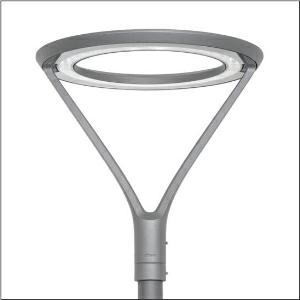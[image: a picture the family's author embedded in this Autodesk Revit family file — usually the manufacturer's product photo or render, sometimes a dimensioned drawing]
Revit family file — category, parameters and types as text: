
# Revit family: dl_r__20___pl1_2s_5xa512832s008p_c84b
name_source: partatom
category: Lighting Fixtures
units: mm (PartAtom-declared; Revit-internal decimal feet)

## family parameters
Cut with Voids When Loaded = No
Host = Face
Light Source = No
Part Type = Normal
Room Calculation Point = No
Round Connector Dimension = Use Diameter
Shared = No

## types (1)
- --- (1 x LED, 4250 lm, 43.6 W, 2200K)
    Apparent Load = 44 VA
    CIE Flux Codes = 33 78 99 100 100
    Color Rendering = 70
    Color Temperature = 2200K
    Default Elevation = 1800 mm
    Description = DL® 20, mast luminaire, primary light control with reflector, highly specular, primary optical cover: cover, of toughened safety glass of clear glass with excellent transmission level, light distribution: PL1.2s, light emission: direct distribution, primary light characteristic: symmetric, installation type: post-top, LED, High Power LED, rated luminous flux: 4.210lm, luminous efficacy: 80lm/W, light colour: 722, colour temperature: 2200K, control gear: ECG Plus, control: flexible luminous flux parameterisation, time-dependent luminous flux control, constant luminous flux control, digital communication interface, power reduction, overheat protection, electronic power reduction, mains connection: 230..240V, 50/60Hz, connection cable pre-assembled, cable length: 5m, start of lifetime: 53W, end of service life: 54W, reduction: 24W, luminaire housing, upper part, of cast aluminium, powder-coated, Siteco® metallic grey (DB 702S), diameter: 690mm, height: 690mm, spigot size: 76mm (post-top), luminaire housing, of cast aluminium, powder-coated, Siteco® metallic grey (DB 702S), equipment: Power, protection rating (complete): IP66, insulation class (complete): insulation class II (safety insulation), certification: CE, ENEC, VDE, impact resistance: IK08, permissible operating ambient temperature: -25..+30°C, standard-compliant lighting for roads and squares, packaging unit: 1 piece

Light Distribution: PL1.2s
    Height = 690 mm
    Lamp = 1 x LED
    Lamp Light Flux = 4250 lm
    Lamp Power = 43.6 W
    Lamp count = 1
    Length = 690 mm
    Luminous efficacy = 97 lm/W
    Manufacturer = Siteco
    ModVariant = No
    Model = 5XA512832S008P
    Number of Poles = 1
    OnlyDefault = Yes
    Power Factor = 1
    Product Name = DL® 20 | PL1.2s
    Product group = mast luminaire | pylon top
    ProductGroupID = 6100
    Protection Class = Protection class II
    Protection Degree = IP 66
    RLX_Detail_Level = 1
    RLX_Emergency_Light_Flux = 0 lm
    RLX_Emergency_Type = 0
    RLX_Emergency_Type_DB = No
    RlxData = <blob elided: 203837 chars, md5=ff13a084>
    Socket = socket
    Standby Power = 0 W
    System Light Flux = 4250 lm
    System Power = 44 W
    Type Comments = factory setting: luminous flux: 100 % | dim-lin: 254 | 587 mA
    Type Image = l_1006001.jpg
    URL = http://relux.com
    VarID = @adj_045991
    Voltage = 0 V
    Weight = 0.00 kg
    Width = 0 mm  [stored 0 ft]

note: [stored X ft] marks values corroborated as IEEE doubles in the binary element streams (Revit-internal decimal feet)

## geometry (parser evidence)
native form markers: Blend x4, Sweep x9
no freeform markers — native parametric forms only
